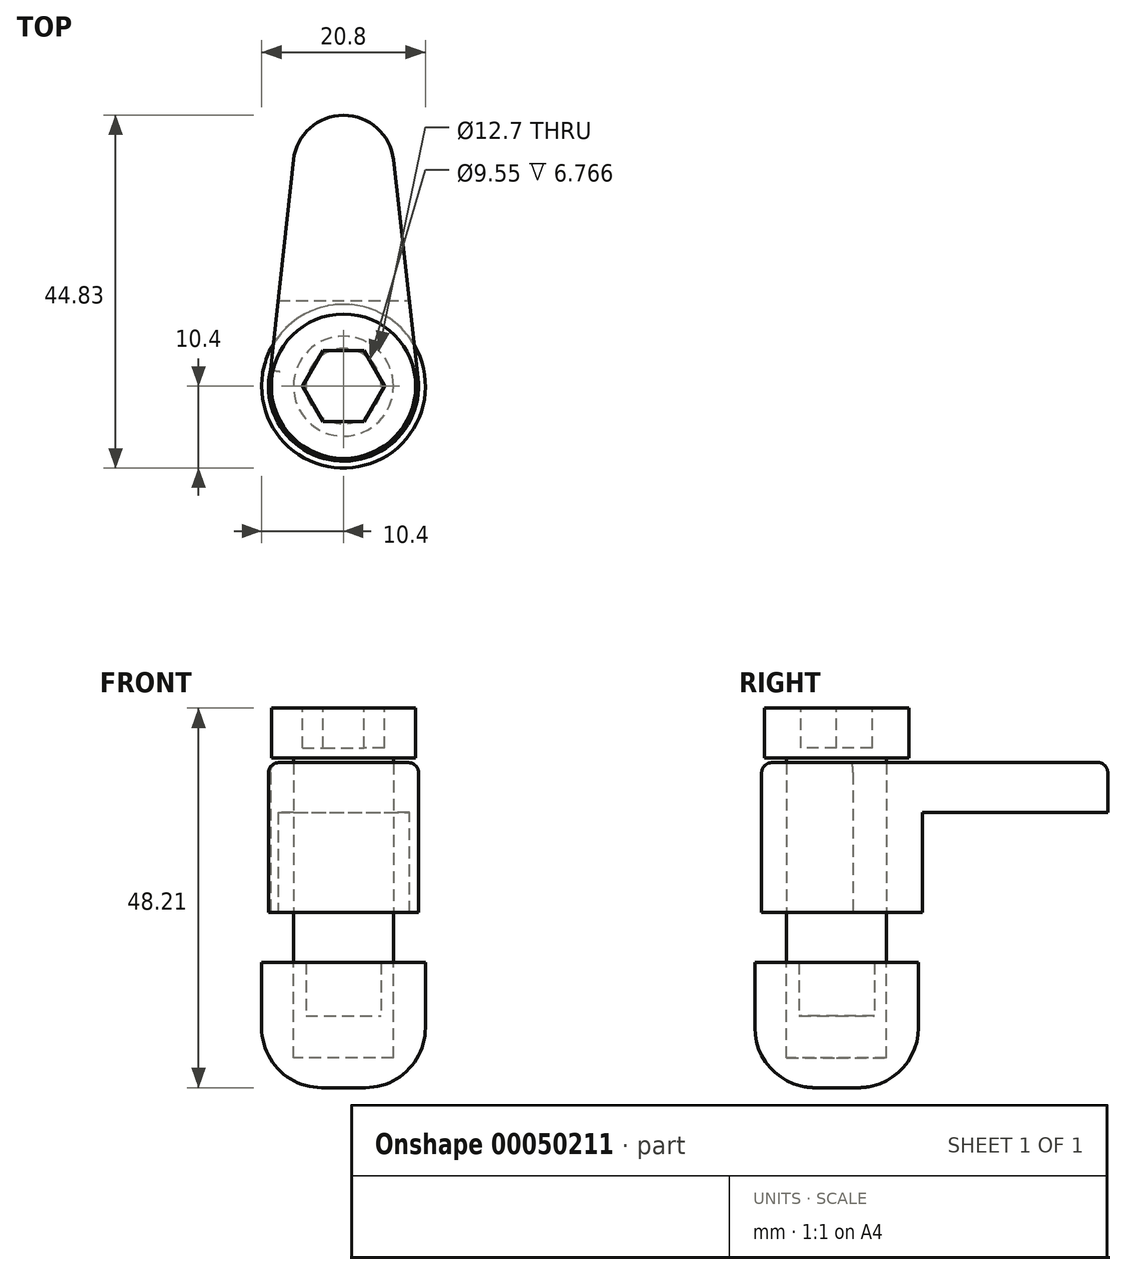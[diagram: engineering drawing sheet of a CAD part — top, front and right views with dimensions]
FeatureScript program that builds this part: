
annotation { "Feature Type Name" : "Feature", "Feature Type Description" : "" }
export const myFeature = defineFeature(function(context is Context, id is Id, definition is map)
    precondition{}
    {
        {
            var Q0;
            Q0=qCreatedBy(makeId("Top.planeOp"),FACE);
            var sketch = newSketch(context, id + "F0", { "sketchPlane" : qUnion([Q0])});
            skCircle(sketch, "E0", {"center": v(0, 0) * mm, "radius": 6.35 * mm});
            skCircle(sketch, "E1", {"center": v(0, 0) * mm, "radius": 9.53 * mm});
            skLineSegment(sketch, "E2", {"start": v(-9.53, 0) * mm, "end": v(-6.35, 28.76) * mm});
            skLineSegment(sketch, "E3", {"start": v(6.35, 28.76) * mm, "end": v(9.59, 0) * mm});
            skArc(sketch, "E4", {"start": v(6.35, 28.76) * mm, "mid": v(0, 34.43) * mm, "end": v(-6.35, 28.76) * mm});
            skSolve(sketch);
        }
        {
            var Q0;
            Q0 = qSketchRegion(id + "F0", true);
            extrude(context, id + "F1", {"entities" : qUnion([Q0]), "depth" : 19.05 * mm});
        }
        {
            var Q0;
            Q0=qCreatedBy(makeId("Right.planeOp"),FACE);
            var sketch = newSketch(context, id + "F2", { "sketchPlane" : qUnion([Q0])});
            skLineSegment(sketch, "E5", {"start": v(10.9, 0) * mm, "end": v(10.9, 12.7) * mm});
            skLineSegment(sketch, "E6", {"start": v(10.9, 12.7) * mm, "end": v(44.38, 12.7) * mm});
            skLineSegment(sketch, "E7", {"start": v(44.38, 12.7) * mm, "end": v(44.38, 0) * mm});
            skLineSegment(sketch, "E8", {"start": v(44.38, 0) * mm, "end": v(10.9, 0) * mm});
            skSolve(sketch);
        }
        {
            var Q0;
            Q0 = qSketchRegion(id + "F2", true);
            extrude(context, id + "F3", {"entities" : qUnion([Q0]), "operationType" : NewBodyOperationType.REMOVE, "oppositeDirection" : true, "depth" : 25.4 * mm, "hasSecondDirection" : true, "secondDirectionOppositeDirection" : false, "secondDirectionDepth" : 25.4 * mm});
        }
        {
            var Q0;
            Q0=makeQuery(id+"F1.opExtrude","CAP_EDGE",EDGE,{"disambiguationData":[OSD([sQuery(id+"F0.wireOp",EDGE,"E3")])],"isStart":false});
            var Q1;
            Q1=makeQuery(id+"F1.opExtrude","CAP_EDGE",EDGE,{"disambiguationData":[OSD([sQuery(id+"F0.wireOp",EDGE,"E4")])],"isStart":false});
            var Q2;
            Q2=makeQuery(id+"F1.opExtrude","CAP_EDGE",EDGE,{"disambiguationData":[OSD([sQuery(id+"F0.wireOp",EDGE,"E2")])],"isStart":false});
            var Q3;
            Q3=makeQuery(id+"F1.opExtrude","CAP_EDGE",EDGE,{"disambiguationData":[OSD([sQuery(id+"F0.wireOp",EDGE,"E1")])],"isStart":false});
            fillet(context, id + "F4", {"entities" : qUnion([Q0, Q1, Q2, Q3]), "radius" : 1.27 * mm, "tangentPropagation" : true, "allowEdgeOverflow" : false});
        }
        {
            var Q0;
            Q0=qCreatedBy(makeId("Right.planeOp"),FACE);
            var sketch = newSketch(context, id + "F5", { "sketchPlane" : qUnion([Q0])});
            skLineSegment(sketch, "E9", {"start": v(0, -18.5) * mm, "end": v(6.35, -18.5) * mm});
            skLineSegment(sketch, "E10", {"start": v(6.35, -18.5) * mm, "end": v(6.35, 19.6) * mm});
            skLineSegment(sketch, "E11", {"start": v(6.35, 19.6) * mm, "end": v(9.17, 19.6) * mm});
            skLineSegment(sketch, "E12", {"start": v(9.17, 19.6) * mm, "end": v(9.17, 25.96) * mm});
            skLineSegment(sketch, "E13", {"start": v(9.17, 25.96) * mm, "end": v(0, 25.96) * mm});
            skLineSegment(sketch, "E14", {"start": v(0, 25.96) * mm, "end": v(0, -18.5) * mm});
            skLineSegment(sketch, "E15", {"start": v(0, 35.01) * mm, "end": v(0, -34.72) * mm, "construction": true});
            skSolve(sketch);
        }
        {
            var Q0;
            Q0 = qSketchRegion(id + "F5", true);
            var Q1;
            Q1=sQuery(id+"F5.wireOp",EDGE,"E15");
            revolve(context, id + "F6", {"entities" : qUnion([Q0]), "axis" : qUnion([Q1]), "revolveType" : RevolveType.FULL});
        }
        {
            var Q0;
            Q0=makeQuery(id+"F6.opRevolve","SWEPT_FACE",FACE,{"disambiguationData":[OSD([sQuery(id+"F5.wireOp",EDGE,"E13")])]});
            var sketch = newSketch(context, id + "F7", { "sketchPlane" : qUnion([Q0])});
            skCircle(sketch, "E16.cCircle", {"center": v(0, 0) * mm, "radius": 5.21 * mm, "construction": true});
            skLineSegment(sketch, "E16.0", {"start": v(5.21, 0) * mm, "end": v(2.6, -4.52) * mm});
            skLineSegment(sketch, "E16.1", {"start": v(2.6, -4.52) * mm, "end": v(-2.6, -4.52) * mm});
            skLineSegment(sketch, "E16.2", {"start": v(-2.6, -4.52) * mm, "end": v(-5.21, 0) * mm});
            skLineSegment(sketch, "E16.3", {"start": v(-5.21, 0) * mm, "end": v(-2.6, 4.52) * mm});
            skLineSegment(sketch, "E16.4", {"start": v(-2.6, 4.52) * mm, "end": v(2.6, 4.52) * mm});
            skLineSegment(sketch, "E16.5", {"start": v(2.6, 4.52) * mm, "end": v(5.21, 0) * mm});
            skSolve(sketch);
        }
        {
            var Q0;
            Q0 = qSketchRegion(id + "F7", true);
            extrude(context, id + "F8", {"entities" : qUnion([Q0]), "operationType" : NewBodyOperationType.REMOVE, "oppositeDirection" : true, "depth" : 5.08 * mm});
        }
        {
            var Q0;
            Q0=qCreatedBy(makeId("Front.planeOp"),FACE);
            var sketch = newSketch(context, id + "F9", { "sketchPlane" : qUnion([Q0])});
            skLineSegment(sketch, "E17", {"start": v(0, -32.93) * mm, "end": v(0, 33.82) * mm, "construction": true});
            skSolve(sketch);
        }
        {
            var Q0;
            Q0=qCreatedBy(makeId("Front.planeOp"),FACE);
            var sketch = newSketch(context, id + "F10", { "sketchPlane" : qUnion([Q0])});
            skLineSegment(sketch, "E18", {"start": v(10.4, -14.63) * mm, "end": v(10.4, -6.35) * mm});
            skLineSegment(sketch, "E19", {"start": v(10.4, -6.35) * mm, "end": v(4.78, -6.35) * mm});
            skLineSegment(sketch, "E20", {"start": v(4.78, -6.35) * mm, "end": v(4.78, -13.12) * mm});
            skLineSegment(sketch, "E21", {"start": v(4.78, -13.12) * mm, "end": v(0, -13.12) * mm});
            skLineSegment(sketch, "E22", {"start": v(0, -13.12) * mm, "end": v(0, -22.2) * mm});
            skLineSegment(sketch, "E23", {"start": v(0, -22.2) * mm, "end": v(2.64, -22.25) * mm});
            skPoint(sketch, "E24.visualSharp", {"position": v(10.4, -22.39) * mm});
            skArc(sketch, "E24.filletArc", {"start": v(2.64, -22.25) * mm, "mid": v(8.12, -20.06) * mm, "end": v(10.4, -14.63) * mm});
            skSolve(sketch);
        }
        {
            var Q0;
            Q0 = qSketchRegion(id + "F10", true);
            var Q1;
            Q1=sQuery(id+"F9.wireOp",EDGE,"E17");
            revolve(context, id + "F11", {"entities" : qUnion([Q0]), "axis" : qUnion([Q1]), "revolveType" : RevolveType.FULL});
        }
    });
